# Revit family: Water_Heater_Manifolds-Navien-NFB-Primary-02
name_source: partatom
category: Pipe Fittings
revit_build: Autodesk Revit 2016 (Build: 20150220_1215(x64)
units: mm (PartAtom-declared; Revit-internal decimal feet)

## family parameters
Always vertical = Yes
Cut with Voids When Loaded = No
OmniClass Number = 23.60.30.11.14
OmniClass Title = Pipework Fittings
Part Type = Multi Port
Round Connector Dimension = Use Radius
Shared = No
Work Plane-Based = No

## types (1)
- NFB Manifold
    Assembly Code = D3010500
    Boiler Heating Return Connection = 1.3 "
    Boiler Heating Supply Connection = 1.3 "
    Boiler Pump = No
    Description = NFB Primary Manifolds
    Finish = Metal - Navien - Copper
    Heating Return = 1.5 "
    Heating Supply = 1.5 "
    K Coefficient Table = Tee
    Keynote = 22 33 00.A1
    Loss Method = Not Defined
    Manufacturer = Navien, Inc.
    Manufacturer Fax Number = (949) 420-0430
    Model = GFFM-MSOZUS-002
    Product Documentation Link = Contact Navien for Product Documentation
    Product Name = Manifold
    Product Page URL = Contact Navien for Product Documentation
    URL = https://www.navieninc.com
    Version = 2016 - v1.0.a
    Weight = 0.00 lbf

## geometry (parser evidence)
native form markers: Sweep x1
no freeform markers — native parametric forms only
